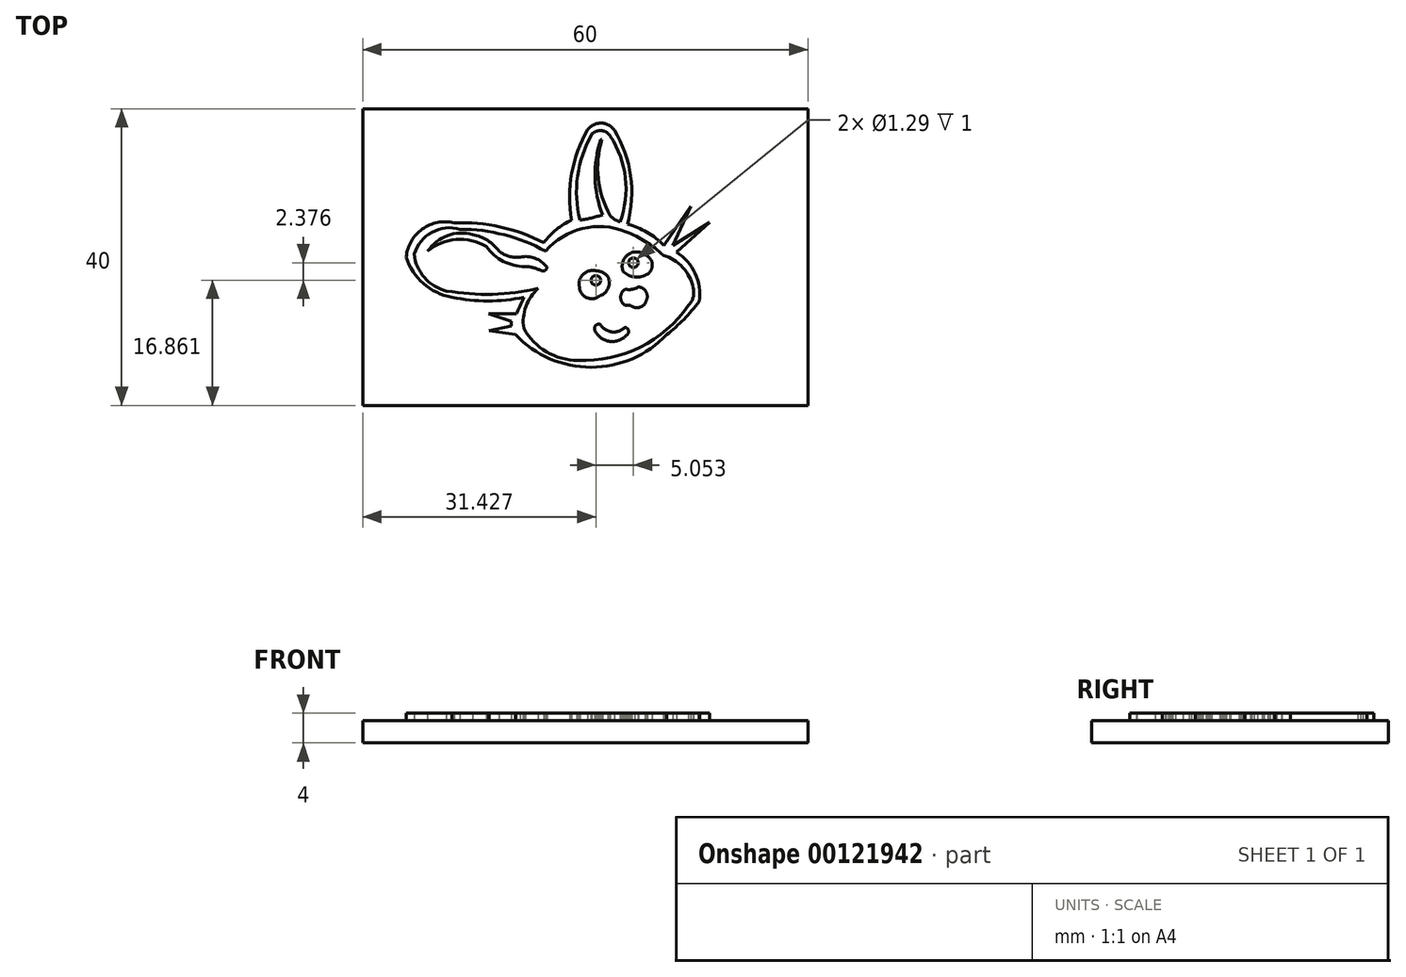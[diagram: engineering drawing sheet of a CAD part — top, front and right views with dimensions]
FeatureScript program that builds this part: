
annotation { "Feature Type Name" : "Feature", "Feature Type Description" : "" }
export const myFeature = defineFeature(function(context is Context, id is Id, definition is map)
    precondition{}
    {
        {
            var Q0;
            Q0=qCreatedBy(makeId("Top.planeOp"),FACE);
            var sketch = newSketch(context, id + "F0", { "sketchPlane" : qUnion([Q0])});
            skLineSegment(sketch, "E0.bottom", {"start": v(30, -20) * mm, "end": v(-30, -20) * mm});
            skLineSegment(sketch, "E0.top", {"start": v(30, 20) * mm, "end": v(-30, 20) * mm});
            skLineSegment(sketch, "E0.left", {"start": v(30, -20) * mm, "end": v(30, 20) * mm});
            skLineSegment(sketch, "E0.right", {"start": v(-30, -20) * mm, "end": v(-30, 20) * mm});
            skPoint(sketch, "E0.middle", {"position": v(0, 0) * mm});
            skSolve(sketch);
        }
        {
            var Q0;
            Q0 = qSketchRegion(id + "F0", true);
            extrude(context, id + "F1", {"entities" : qUnion([Q0]), "depth" : 3 * mm});
        }
        {
            var Q0;
            Q0=makeQuery(id+"F1.opExtrude","CAP_FACE",FACE,{"disambiguationData":[OSD([sQuery(id+"F0.wireOp",EDGE,"E0.bottom"),sQuery(id+"F0.wireOp",EDGE,"E0.top"),sQuery(id+"F0.wireOp",EDGE,"E0.left"),sQuery(id+"F0.wireOp",EDGE,"E0.right")])],"isStart":false});
            var sketch = newSketch(context, id + "F2", { "sketchPlane" : qUnion([Q0])});
            skArc(sketch, "E1", {"start": v(-5.58, 1.93) * mm, "mid": v(-11.45, 4.06) * mm, "end": v(-17.68, 4.6) * mm});
            skArc(sketch, "E2", {"start": v(-17.68, 4.6) * mm, "mid": v(-21.96, 3.78) * mm, "end": v(-24.13, 0) * mm});
            skArc(sketch, "E3", {"start": v(-24.13, 0) * mm, "mid": v(-21.82, -3.58) * mm, "end": v(-17.97, -5.41) * mm});
            skArc(sketch, "E4", {"start": v(-17.97, -5.41) * mm, "mid": v(-13.11, -5.91) * mm, "end": v(-8.25, -5.41) * mm});
            skArc(sketch, "E5", {"start": v(-9.3, -7.64) * mm, "mid": v(-8.75, -6.54) * mm, "end": v(-8.25, -5.41) * mm});
            skLineSegment(sketch, "E6", {"start": v(-9.3, -7.64) * mm, "end": v(-13, -7.64) * mm});
            skLineSegment(sketch, "E7", {"start": v(-13, -7.64) * mm, "end": v(-10, -8.66) * mm});
            skLineSegment(sketch, "E8", {"start": v(-10, -8.66) * mm, "end": v(-10, -9.32) * mm});
            skLineSegment(sketch, "E9", {"start": v(-10, -9.32) * mm, "end": v(-12.98, -9.96) * mm});
            skLineSegment(sketch, "E10", {"start": v(-12.98, -9.96) * mm, "end": v(-9.4, -10.47) * mm});
            skArc(sketch, "E11", {"start": v(-9.4, -10.47) * mm, "mid": v(0.78, -14.86) * mm, "end": v(10.96, -10.47) * mm});
            skArc(sketch, "E12", {"start": v(10.96, -10.47) * mm, "mid": v(13.3, -8.38) * mm, "end": v(15.35, -6) * mm});
            skArc(sketch, "E13", {"start": v(15.35, -6) * mm, "mid": v(14.82, -2.21) * mm, "end": v(12.28, 0.65) * mm});
            skArc(sketch, "E14", {"start": v(-5.36, 0.8) * mm, "mid": v(-10.93, 3) * mm, "end": v(-16.88, 3.75) * mm});
            skArc(sketch, "E15", {"start": v(-16.88, 3.75) * mm, "mid": v(-20.66, 3.34) * mm, "end": v(-23.07, 0.4) * mm});
            skArc(sketch, "E16", {"start": v(-23.07, 0.4) * mm, "mid": v(-21.68, -2.78) * mm, "end": v(-18.71, -4.57) * mm});
            skArc(sketch, "E17", {"start": v(-18.71, -4.57) * mm, "mid": v(-12.5, -5) * mm, "end": v(-6.33, -4.23) * mm});
            skArc(sketch, "E18", {"start": v(-6.33, -4.23) * mm, "mid": v(-8.01, -6.67) * mm, "end": v(-8.3, -9.62) * mm});
            skArc(sketch, "E19", {"start": v(-8.3, -9.62) * mm, "mid": v(-5.24, -12.77) * mm, "end": v(-1, -13.92) * mm});
            skArc(sketch, "E20", {"start": v(-1, -13.92) * mm, "mid": v(7.42, -12.15) * mm, "end": v(13.93, -6.5) * mm});
            skArc(sketch, "E21", {"start": v(13.93, -6.5) * mm, "mid": v(14.54, -5.42) * mm, "end": v(14.54, -4.17) * mm});
            skArc(sketch, "E22", {"start": v(14.54, -4.17) * mm, "mid": v(13.14, -1.4) * mm, "end": v(10.52, 0.26) * mm});
            skArc(sketch, "E23", {"start": v(10.52, 0.26) * mm, "mid": v(8.14, 2.08) * mm, "end": v(5.48, 3.43) * mm});
            skArc(sketch, "E24", {"start": v(10.59, 1.6) * mm, "mid": v(8.33, 3.35) * mm, "end": v(5.7, 4.44) * mm});
            skArc(sketch, "E25", {"start": v(5.48, 3.43) * mm, "mid": v(-0.36, 3.84) * mm, "end": v(-5.36, 0.8) * mm});
            skArc(sketch, "E26", {"start": v(-1.83, 4.99) * mm, "mid": v(-3.9, 3.7) * mm, "end": v(-5.58, 1.93) * mm});
            skArc(sketch, "E27", {"start": v(0.34, 17.2) * mm, "mid": v(-1.84, 11.29) * mm, "end": v(-1.83, 4.99) * mm});
            skArc(sketch, "E28", {"start": v(3.9, 17.12) * mm, "mid": v(2.14, 18.07) * mm, "end": v(0.34, 17.2) * mm});
            skArc(sketch, "E29", {"start": v(5.7, 4.44) * mm, "mid": v(6.12, 10.97) * mm, "end": v(3.9, 17.12) * mm});
            skArc(sketch, "E30", {"start": v(4.67, 4.74) * mm, "mid": v(5.4, 10.67) * mm, "end": v(3.39, 16.3) * mm});
            skArc(sketch, "E31", {"start": v(3.39, 16.3) * mm, "mid": v(2.22, 17.05) * mm, "end": v(0.9, 16.59) * mm});
            skArc(sketch, "E32", {"start": v(0.9, 16.59) * mm, "mid": v(-1.04, 10.93) * mm, "end": v(-0.7, 4.96) * mm});
            skArc(sketch, "E33", {"start": v(-0.7, 4.96) * mm, "mid": v(0.82, 5.28) * mm, "end": v(2.32, 5.69) * mm});
            skArc(sketch, "E34", {"start": v(2.1, 15.86) * mm, "mid": v(1.32, 10.75) * mm, "end": v(2.32, 5.69) * mm});
            skArc(sketch, "E35", {"start": v(2.24, 15.86) * mm, "mid": v(1.75, 10.6) * mm, "end": v(3.36, 5.57) * mm});
            skArc(sketch, "E36", {"start": v(3.36, 5.57) * mm, "mid": v(3.97, 5.08) * mm, "end": v(4.67, 4.74) * mm});
            skLineSegment(sketch, "E37", {"start": v(10.59, 1.6) * mm, "end": v(14.19, 6.82) * mm});
            skLineSegment(sketch, "E38", {"start": v(14.19, 6.82) * mm, "end": v(11.77, 1.6) * mm});
            skLineSegment(sketch, "E39", {"start": v(11.77, 1.6) * mm, "end": v(16.73, 4.7) * mm});
            skLineSegment(sketch, "E40", {"start": v(16.73, 4.7) * mm, "end": v(12.28, 0.65) * mm});
            skArc(sketch, "E41", {"start": v(2.02, -9.07) * mm, "mid": v(3.6, -10.1) * mm, "end": v(5.36, -9.46) * mm});
            skArc(sketch, "E42", {"start": v(1.33, -9.97) * mm, "mid": v(3.3, -11.37) * mm, "end": v(5.58, -10.53) * mm});
            skArc(sketch, "E43", {"start": v(2.02, -9.07) * mm, "mid": v(1.35, -9.28) * mm, "end": v(1.33, -9.97) * mm});
            skArc(sketch, "E44", {"start": v(5.58, -10.53) * mm, "mid": v(5.83, -9.92) * mm, "end": v(5.36, -9.46) * mm});
            skArc(sketch, "E45", {"start": v(1.43, -1.85) * mm, "mid": v(-0.27, -2.3) * mm, "end": v(-0.8, -3.99) * mm});
            skArc(sketch, "E46", {"start": v(-0.8, -3.99) * mm, "mid": v(0.17, -5.46) * mm, "end": v(1.92, -5.24) * mm});
            skArc(sketch, "E47", {"start": v(3.03, -2.6) * mm, "mid": v(2.31, -2.05) * mm, "end": v(1.43, -1.85) * mm});
            skArc(sketch, "E48", {"start": v(1.92, -5.24) * mm, "mid": v(3.08, -4.18) * mm, "end": v(3.03, -2.6) * mm});
            skArc(sketch, "E49", {"start": v(6.64, 0.69) * mm, "mid": v(5.21, -0.29) * mm, "end": v(5.13, -2) * mm});
            skArc(sketch, "E50", {"start": v(5.13, -2) * mm, "mid": v(6.71, -2.68) * mm, "end": v(8.4, -2.3) * mm});
            skArc(sketch, "E51", {"start": v(8.4, -2.3) * mm, "mid": v(9.02, -0.9) * mm, "end": v(8.08, 0.28) * mm});
            skArc(sketch, "E52", {"start": v(8.08, 0.28) * mm, "mid": v(7.4, 0.63) * mm, "end": v(6.64, 0.69) * mm});
            skCircle(sketch, "E53", {"center": v(1.43, -3.14) * mm, "radius": 0.64 * mm});
            skCircle(sketch, "E54", {"center": v(6.48, -0.76) * mm, "radius": 0.64 * mm});
            skArc(sketch, "E55", {"start": v(5.38, -4.33) * mm, "mid": v(6.3, -4.36) * mm, "end": v(7.17, -4.02) * mm});
            skArc(sketch, "E56", {"start": v(8.24, -5.84) * mm, "mid": v(8.18, -4.65) * mm, "end": v(7.17, -4.02) * mm});
            skArc(sketch, "E57", {"start": v(6.07, -6.5) * mm, "mid": v(7.34, -6.77) * mm, "end": v(8.24, -5.84) * mm});
            skArc(sketch, "E58", {"start": v(5.38, -4.33) * mm, "mid": v(4.76, -5.43) * mm, "end": v(5.38, -6.53) * mm});
            skLineSegment(sketch, "E59", {"start": v(5.38, -6.53) * mm, "end": v(6.07, -6.5) * mm});
            skArc(sketch, "E60", {"start": v(-13.35, 1.42) * mm, "mid": v(-17.4, 2.36) * mm, "end": v(-21.25, 0.78) * mm});
            skArc(sketch, "E61", {"start": v(-15.18, 3.02) * mm, "mid": v(-18.58, 2.9) * mm, "end": v(-21.25, 0.78) * mm});
            skArc(sketch, "E62", {"start": v(-11.61, 0.78) * mm, "mid": v(-13.18, 2.24) * mm, "end": v(-15.18, 3.02) * mm});
            skArc(sketch, "E63", {"start": v(-11.61, 0.78) * mm, "mid": v(-10.28, 0.1) * mm, "end": v(-8.78, 0) * mm});
            skArc(sketch, "E64", {"start": v(-5.17, -1.37) * mm, "mid": v(-6.78, -0.16) * mm, "end": v(-8.78, 0) * mm});
            skArc(sketch, "E65", {"start": v(-13.35, 1.42) * mm, "mid": v(-11.05, -0.57) * mm, "end": v(-8.1, -1.28) * mm});
            skArc(sketch, "E66", {"start": v(-5.95, -1.83) * mm, "mid": v(-7, -1.43) * mm, "end": v(-8.1, -1.28) * mm});
            skArc(sketch, "E67", {"start": v(-5.95, -1.83) * mm, "mid": v(-5.44, -1.81) * mm, "end": v(-5.17, -1.37) * mm});
            skLineSegment(sketch, "E68", {"start": v(2.1, 15.86) * mm, "end": v(2.24, 15.86) * mm});
            skSolve(sketch);
        }
        {
            var Q0;
            Q0 = qSketchRegion(id + "F2", true);
            var Q1;
            Q1=makeQuery(id+"F2.imprint","IMPRINT",FACE,{"disambiguationData":[TD([[makeQuery(id+"F2.imprint","IMPRINT",EDGE,{"derivedFrom":sQuery(id+"F2.wireOp",EDGE,"E45")}),1.0]])]});
            var Q2;
            Q2=makeQuery(id+"F2.imprint","IMPRINT",FACE,{"disambiguationData":[TD([[makeQuery(id+"F2.imprint","IMPRINT",EDGE,{"derivedFrom":sQuery(id+"F2.wireOp",EDGE,"E49")}),1.0]])]});
            var Q3;
            Q3=makeQuery(id+"F2.imprint","IMPRINT",FACE,{"disambiguationData":[TD([[makeQuery(id+"F2.imprint","IMPRINT",EDGE,{"derivedFrom":sQuery(id+"F2.wireOp",EDGE,"E55")}),-1.0]])]});
            var Q4;
            Q4=makeQuery(id+"F2.imprint","IMPRINT",FACE,{"disambiguationData":[TD([[makeQuery(id+"F2.imprint","IMPRINT",EDGE,{"derivedFrom":sQuery(id+"F2.wireOp",EDGE,"E41")}),-1.0]])]});
            var Q5;
            Q5=makeQuery(id+"F2.imprint","IMPRINT",FACE,{"disambiguationData":[TD([[makeQuery(id+"F2.imprint","IMPRINT",EDGE,{"derivedFrom":sQuery(id+"F2.wireOp",EDGE,"E60")}),-1.0]])]});
            extrude(context, id + "F3", {"entities" : qUnion([Q0, Q1, Q2, Q3, Q4, Q5]), "operationType" : NewBodyOperationType.ADD, "depth" : 1 * mm});
        }
    });
